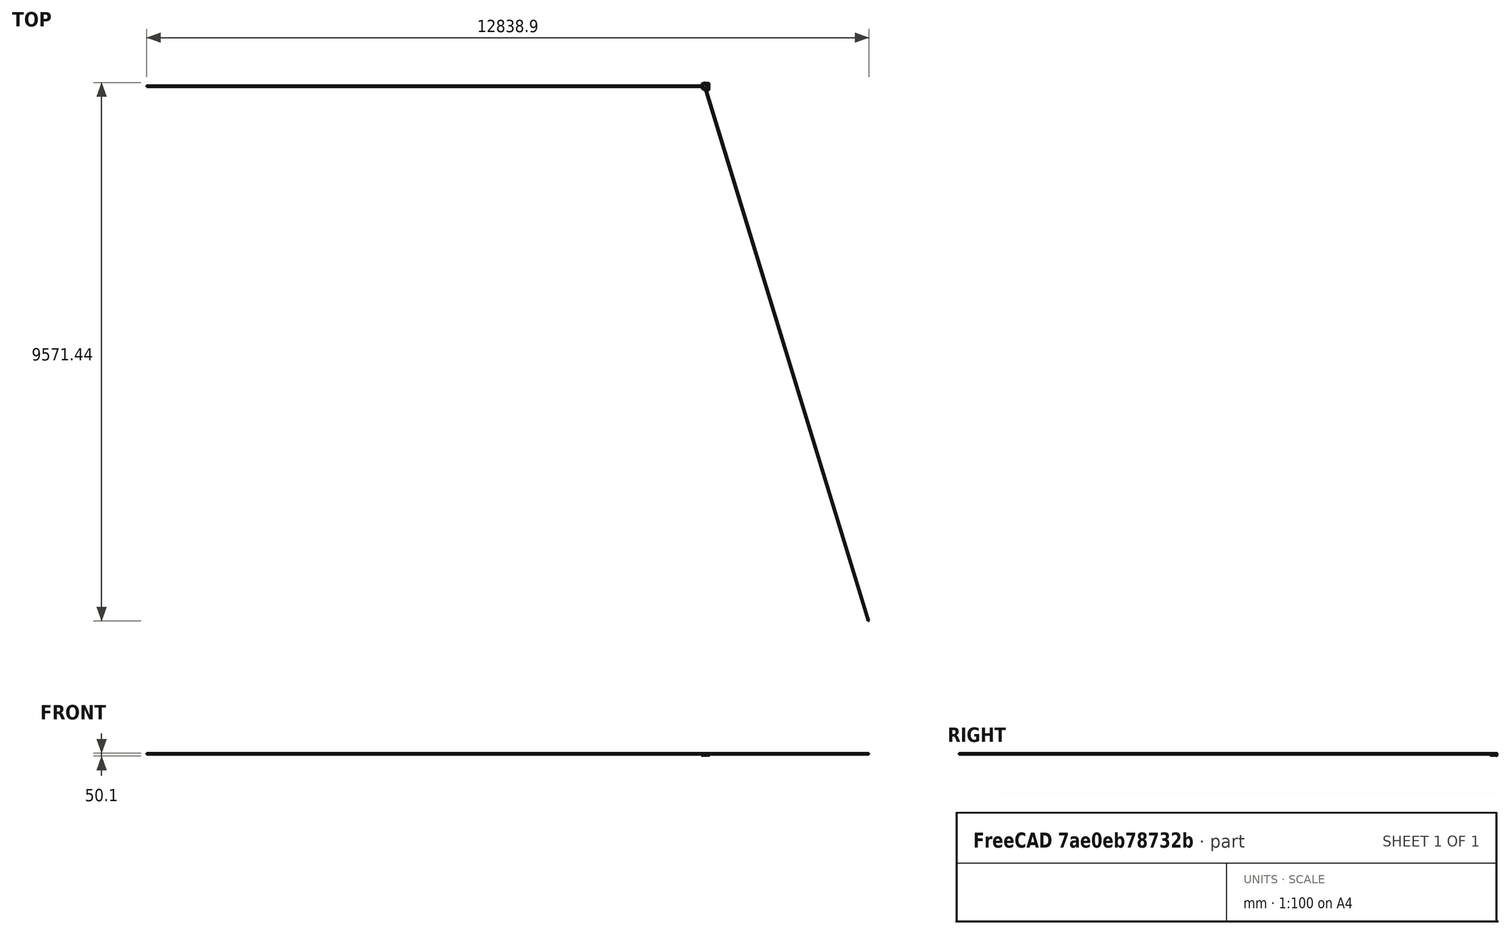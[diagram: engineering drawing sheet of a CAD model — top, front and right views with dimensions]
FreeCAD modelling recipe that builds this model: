
FCSTD DOCUMENT  (FreeCAD 0.16R)
Label: chainguard25TRearRev3
License: All rights reserved
LicenseURL: http://en.wikipedia.org/wiki/All_rights_reserved
objects: Sketcher::SketchObject×14, PartDesign::Pocket×7, PartDesign::Pad×6, Part::FeaturePython×4, Mesh::Feature×4, PartDesign::Fillet×2
note: 46 computed .brp shape members not serialized (recipe doc carries the construction recipe); baked Part::Feature solids carry a one-line shape summary decoded from their .brp

FEATURE [Sketcher::SketchObject] Sketch001
  sketch-geometry (7):
    g0: LineSegment StartX=60 StartY=64 StartZ=0 EndX=0 EndY=64 EndZ=0
    g1: LineSegment StartX=60 StartY=-64 StartZ=0 EndX=0 EndY=-64 EndZ=0
    g2: ArcOfCircle CenterX=8.21903e-05 CenterY=0 CenterZ=0 NormalX=0 NormalY=0 NormalZ=1 Radius=64 StartAngle=1.5708 EndAngle=4.71239
    g3: Circle CenterX=0 CenterY=0 CenterZ=0 NormalX=0 NormalY=0 NormalZ=1 Radius=45
    g4: ArcOfCircle CenterX=60 CenterY=51 CenterZ=0 NormalX=0 NormalY=0 NormalZ=1 Radius=13 StartAngle=0 EndAngle=1.5708
    g5: ArcOfCircle CenterX=60 CenterY=-51 CenterZ=0 NormalX=0 NormalY=0 NormalZ=1 Radius=13 StartAngle=4.71239 EndAngle=6.28319
    g6: LineSegment StartX=73 StartY=51 StartZ=0 EndX=73 EndY=-51 EndZ=0
  constraints (23):
    c: Horizontal(g0)
    c: Horizontal(g1)
    c: Coincident(g2,g1)
    c: Coincident(g0,g2)
    c: DistanceX(g1,g0) = 0
    c: Equal(g0,g1)
    c: DistanceY(g1,g0) = 128
    c: Radius(g2) = 64
    c: Symmetric(g1,g0,g-1)
    c: Radius(g3) = 45
    c: Coincident(g3,g-1)
    c: PointOnObject(g4,g0)
    c: Radius(g4) = 13
    c: DistanceX(g0,g0) = 60
    c: Equal(g5,g4)
    c: Vertical(g6)
    c: DistanceX(g-1,g6) = 73
    c: Symmetric(g6,g6,g-1)
    c: DistanceY(g6,g6) = 102
    c: Coincident(g4,g6)
    c: Coincident(g5,g6)
    c: Coincident(g1,g5)
    c: Coincident(g0,g4)
FEATURE [PartDesign::Pad] Pad  label="Faceplate"
  Length = 1.12
  Length2 = 100
  Reversed = true
  Sketch = -> Sketch001
  Type = 0
FEATURE [Sketcher::SketchObject] Sketch002
  sketch-geometry (8):
    g0: LineSegment StartX=60 StartY=64 StartZ=0 EndX=0 EndY=64 EndZ=0
    g1: LineSegment StartX=60 StartY=-64 StartZ=0 EndX=0 EndY=-64 EndZ=0
    g2: ArcOfCircle CenterX=6.44712e-05 CenterY=0 CenterZ=0 NormalX=0 NormalY=0 NormalZ=1 Radius=64 StartAngle=1.5708 EndAngle=4.71239
    g3: LineSegment StartX=0 StartY=62 StartZ=0 EndX=60 EndY=62 EndZ=0
    g4: LineSegment StartX=0 StartY=-62 StartZ=0 EndX=60 EndY=-62 EndZ=0
    g5: LineSegment StartX=60 StartY=64 StartZ=0 EndX=60 EndY=62 EndZ=0
    g6: LineSegment StartX=60 StartY=-62 StartZ=0 EndX=60 EndY=-64 EndZ=0
    g7: ArcOfCircle CenterX=1.45954e-05 CenterY=0 CenterZ=0 NormalX=0 NormalY=0 NormalZ=1 Radius=62 StartAngle=1.5708 EndAngle=4.71239
  constraints (25):
    c: Horizontal(g0)
    c: Horizontal(g1)
    c: Coincident(g2,g1)
    c: Coincident(g0,g2)
    c: DistanceX(g1,g0) = 0
    c: Equal(g0,g1)
    c: DistanceY(g1,g0) = 128
    c: Radius(g2) = 64
    c: Symmetric(g1,g0,g-1)
    c: Radius(g7) = 62
    c: Parallel(g0,g3)
    c: DistanceY(g3,g0) = 2
    c: DistanceY(g1,g4) = 2
    c: Parallel(g4,g1)
    c: DistanceX(g0,g3) = 0
    c: DistanceX(g4) = 0
    c: DistanceX(g0) = 60
    c: Equal(g3,g0)
    c: Equal(g4,g0)
    c: Coincident(g4,g6)
    c: Coincident(g6,g1)
    c: Coincident(g5,g3)
    c: Coincident(g5,g0)
    c: Coincident(g7,g3)
    c: Coincident(g7,g4)
FEATURE [PartDesign::Pad] Pad001  label="Connector"
  Length = 10
  Length2 = 100
  Sketch = -> Sketch002
  Type = 0
FEATURE [Sketcher::SketchObject] Sketch011
  Placement = pos=(0,64,0) rot=(0,0.707107,0.707107;3.14159rad)
  Support = -> Pad001 [Face1]
  sketch-geometry (4):
    g0: LineSegment StartX=-52 StartY=11 StartZ=0 EndX=-64.6477 EndY=14.0061 EndZ=0
    g1: LineSegment StartX=-64.6477 StartY=14.0061 StartZ=0 EndX=-60.9272 EndY=1.54985 EndZ=0
    g2: LineSegment StartX=-60.9272 StartY=1.54985 StartZ=0 EndX=-52 EndY=11 EndZ=0
    g3: Circle [constr] CenterX=-59.1916 CenterY=8.85198 CenterZ=0 NormalX=0 NormalY=0 NormalZ=1 Radius=7.50555
  constraints (14):
    c: Coincident(g0,g1)
    c: Coincident(g1,g2)
    c: Coincident(g2,g0)
    c: Equal(g0,g1)
    c: Equal(g0,g2)
    c: PointOnObject(g0,g3)
    c: PointOnObject(g1,g3)
    c: PointOnObject(g2,g3)
    c: DistanceY(g-1,g0) = 11
    c: DistanceX(g0,g-1) = 52
    c: Equal(g2,g0)
    c: Equal(g0,g1)
    c: Distance(g2) = 13
    c: Angle(g0) = 2.90824
FEATURE [PartDesign::Pocket] Pocket005  label="Bevel_connector"
  Length = 5
  Sketch = -> Sketch011
  Type = 1
FEATURE [Sketcher::SketchObject] Sketch017
  sketch-geometry (5):
    g0: LineSegment [constr] StartX=-4 StartY=2 StartZ=0 EndX=-27.8283 EndY=79.9388 EndZ=0
    g1: LineSegment StartX=-5.80278 StartY=67.752 StartZ=0 EndX=-39.2735 EndY=57.5189 EndZ=0
    g2: LineSegment StartX=-39.2735 StartY=57.5189 StartZ=0 EndX=-37.5192 EndY=51.7811 EndZ=0
    g3: LineSegment StartX=-37.5192 StartY=51.7811 StartZ=0 EndX=-4.04855 EndY=62.0141 EndZ=0
    g4: LineSegment StartX=-4.04855 StartY=62.0141 StartZ=0 EndX=-5.80278 EndY=67.752 EndZ=0
  constraints (15):
    c: DistanceY(g-1,g0) = 2
    c: DistanceX(g-1,g0) = -4
    c: Angle(g0) = 1.8675
    c: Coincident(g1,g2)
    c: Coincident(g2,g3)
    c: Coincident(g3,g4)
    c: Coincident(g1,g4)
    c: Parallel(g2,g4)
    c: Parallel(g1,g3)
    c: Perpendicular(g2,g1)
    c: Distance(g4) = 6
    c: Distance(g1) = 35
    c: Symmetric(g3,g2,g0)
    c: Distance(g-1,g1) = 68
    c: Distance(g0) = 81.5
FEATURE [Sketcher::SketchObject] Sketch020
  sketch-geometry (4):
    g0: LineSegment StartX=67 StartY=35 StartZ=0 EndX=73 EndY=35 EndZ=0
    g1: LineSegment StartX=73 StartY=35 StartZ=0 EndX=73 EndY=-25 EndZ=0
    g2: LineSegment StartX=73 StartY=-25 StartZ=0 EndX=67 EndY=-25 EndZ=0
    g3: LineSegment StartX=67 StartY=-25 StartZ=0 EndX=67 EndY=35 EndZ=0
  constraints (12):
    c: Coincident(g0,g1)
    c: Coincident(g1,g2)
    c: Coincident(g2,g3)
    c: Coincident(g3,g0)
    c: Horizontal(g0)
    c: Horizontal(g2)
    c: Vertical(g1)
    c: Vertical(g3)
    c: DistanceX(g-1,g0) = 73
    c: DistanceX(g0,g0) = 6
    c: DistanceY(g-1,g0) = 35
    c: DistanceY(g1,g1) = 60
FEATURE [PartDesign::Pad] Pad004  label="SyncBoss"
  Length = 31
  Length2 = 100
  Sketch = -> Sketch020
  Type = 0
FEATURE [Sketcher::SketchObject] Sketch021
  ExternalGeometry = -> [Pad004]
  Placement = pos=(73,0,0) rot=(0.57735,0.57735,0.57735;2.0944rad)
  Support = -> Pad004 [Face2]
  sketch-geometry (1):
    g0: Circle CenterX=5 CenterY=31 CenterZ=0 NormalX=0 NormalY=0 NormalZ=1 Radius=11.2
  constraints (2):
    c: Symmetric(g-4,g-3,g0)
    c: Radius(g0) = 11.2
FEATURE [PartDesign::Pocket] Pocket  label="SyncHole"
  Length = 5
  Sketch = -> Sketch021
  Type = 1
FEATURE [PartDesign::Pad] Pad005  label="STBoss"
  Length = 31
  Length2 = 1
  Sketch = -> Sketch017
  Type = 4
FEATURE [Sketcher::SketchObject] Sketch022
  ExternalGeometry = -> [Pad005]
  Placement = pos=(-19.4392,63.5829,0) rot=(-0.105093,0.703191,0.703191;3.35101rad)
  Support = -> Pad005 [Face1]
  sketch-geometry (1):
    g0: Circle CenterX=3.24048 CenterY=31 CenterZ=0 NormalX=0 NormalY=0 NormalZ=1 Radius=11.2
  constraints (2):
    c: Symmetric(g-4,g-3,g0)
    c: Radius(g0) = 11.2
FEATURE [PartDesign::Pocket] Pocket006  label="SThole"
  Length = 5
  Sketch = -> Sketch022
  Type = 1
FEATURE [Sketcher::SketchObject] Sketch023
  Placement = pos=(-19.4392,63.5829,0) rot=(-0.105093,0.703191,0.703191;3.35101rad)
  Support = -> Pocket006 [Face1]
  sketch-geometry (3):
    g0: LineSegment StartX=31.754 StartY=21.6568 StartZ=0 EndX=10.7035 EndY=-1 EndZ=0
    g1: LineSegment StartX=10.7035 StartY=-1 StartZ=0 EndX=40.8501 EndY=-7.90189 EndZ=0
    g2: LineSegment StartX=40.8501 StartY=-7.90189 StartZ=0 EndX=31.754 EndY=21.6568 EndZ=0
  constraints (9):
    c: Coincident(g0,g1)
    c: Coincident(g1,g2)
    c: Coincident(g0,g2)
    c: Equal(g0,g2)
    c: Equal(g2,g1)
    c: DistanceY(g0,g-1) = 1
    c: Angle(g1) = -0.225065
    c: Distance(g2) = 30.9266
    c: DistanceX(g-1,g0) = 10.7035
FEATURE [PartDesign::Pocket] Pocket007  label="STbevel1"
  Length = 6
  Sketch = -> Sketch023
  Type = 0
FEATURE [Sketcher::SketchObject] Sketch024
  sketch-geometry (6):
    g0: ArcOfCircle CenterX=0 CenterY=0 CenterZ=0 NormalX=0 NormalY=0 NormalZ=1 Radius=48 StartAngle=1.34179 EndAngle=4.9414
    g1: Circle CenterX=0 CenterY=0 CenterZ=0 NormalX=0 NormalY=0 NormalZ=1 Radius=45
    g2: LineSegment StartX=10.8966 StartY=46.7468 StartZ=0 EndX=65 EndY=35.4994 EndZ=0
    g3: LineSegment StartX=65 StartY=35.5006 StartZ=0 EndX=65 EndY=-35.4994 EndZ=0
    g4: LineSegment StartX=65 StartY=-35.4994 StartZ=0 EndX=10.8966 EndY=-46.7468 EndZ=0
    g5: LineSegment StartX=65 StartY=35.5 StartZ=0 EndX=65 EndY=-35.5 EndZ=0
  constraints (14):
    c: Coincident(g0,g-1)
    c: Radius(g0) = 48
    c: Coincident(g1,g-1)
    c: Radius(g1) = 45
    c: Coincident(g3,g4)
    c: Coincident(g0,g2)
    c: Distance(g3) = 71
    c: DistanceX(g-1,g2) = 65
    c: Equal(g4,g2)
    c: Vertical(g3)
    c: Symmetric(g2,g3,g-1)
    c: Distance(g2) = 55.2601
    c: DistanceY(g-1,g0) = 46.7468
    c: DistanceX(g0) = 10.8966
FEATURE [Sketcher::SketchObject] Sketch026
  sketch-geometry (4):
    g0: LineSegment StartX=0 StartY=47.5 StartZ=0 EndX=73 EndY=35 EndZ=0
    g1: LineSegment StartX=73 StartY=35 StartZ=0 EndX=73 EndY=-35 EndZ=0
    g2: LineSegment StartX=73 StartY=-35 StartZ=0 EndX=0 EndY=-47.5 EndZ=0
    g3: LineSegment StartX=0 StartY=-47.5 StartZ=0 EndX=0 EndY=47.5 EndZ=0
  constraints (11):
    c: Coincident(g0,g1)
    c: Coincident(g1,g2)
    c: Coincident(g2,g3)
    c: Coincident(g3,g0)
    c: Symmetric(g2,g0,g-1)
    c: Symmetric(g2,g0,g-1)
    c: Equal(g0,g2)
    c: Vertical(g1)
    c: DistanceY(g1,g1) = 70
    c: DistanceY(g3,g3) = 95
    c: DistanceX(g-1,g0) = 73
FEATURE [PartDesign::Pad] Pad007  label="FieldStiffener"
  Length = 1
  Length2 = 100
  Sketch = -> Sketch026
  Type = 0
FEATURE [Sketcher::SketchObject] Sketch028
  ExternalGeometry = -> [Pocket]
  Placement = pos=(0,0,31) rot=(0,0,1;0rad)
  Support = -> Pocket [Face5]
  sketch-geometry (2):
    g0: Circle CenterX=70 CenterY=19 CenterZ=0 NormalX=0 NormalY=0 NormalZ=1 Radius=0.8
    g1: Circle CenterX=70 CenterY=-9 CenterZ=0 NormalX=0 NormalY=0 NormalZ=1 Radius=0.8
  constraints (6):
    c: DistanceY(g-4,g0) = 2.8
    c: DistanceX(g0,g-4) = 3
    c: DistanceX(g1,g-6) = 3
    c: DistanceY(g1,g-5) = 2.8
    c: Equal(g1,g0)
    c: Radius(g1) = 0.8
FEATURE [PartDesign::Pocket] Pocket010  label="SyncScrewHoles"
  Length = 15
  Sketch = -> Sketch028
  Type = 0
FEATURE [Sketcher::SketchObject] Sketch029
  ExternalGeometry = -> [Pocket010]
  Placement = pos=(73,0,0) rot=(0.57735,0.57735,0.57735;2.0944rad)
  Support = -> Pocket010 [Face3]
  sketch-geometry (6):
    g0: LineSegment StartX=35 StartY=3 StartZ=0 EndX=22.5 EndY=32 EndZ=0
    g1: LineSegment StartX=22.5 StartY=32 StartZ=0 EndX=-12.5 EndY=32 EndZ=0
    g2: LineSegment StartX=-12.5 StartY=32 StartZ=0 EndX=-25 EndY=3 EndZ=0
    g3: LineSegment StartX=-25 StartY=3 StartZ=0 EndX=-28.2949 EndY=52.1665 EndZ=0
    g4: LineSegment StartX=-28.2949 StartY=52.1665 StartZ=0 EndX=43.0613 EndY=52.1665 EndZ=0
    g5: LineSegment StartX=43.0613 StartY=52.1665 StartZ=0 EndX=35 EndY=3 EndZ=0
  constraints (18):
    c: Coincident(g0,g1)
    c: Horizontal(g1)
    c: Coincident(g1,g2)
    c: Coincident(g2,g3)
    c: Coincident(g3,g4)
    c: Horizontal(g4)
    c: Coincident(g4,g5)
    c: Coincident(g0,g5)
    c: DistanceX(g-4,g0) = 6.3
    c: DistanceX(g1,g-4) = 6.3
    c: DistanceX(g-3,g0) = 0
    c: DistanceX(g2,g-6) = 0
    c: DistanceX(g4,g4) = 71.3562
    c: Distance(g3) = 49.2768
    c: Distance(g5) = 49.823
    c: DistanceY(g-4,g1) = 1
    c: DistanceY(g-6,g2) = 3
    c: DistanceY(g-3,g0) = 3
FEATURE [PartDesign::Pocket] Pocket011  label="SyncBigBevel"
  Length = 5
  Sketch = -> Sketch029
  Type = 1
FEATURE [Sketcher::SketchObject] Sketch
  ExternalGeometry = -> [Pad]
  Support = -> Pad [Face8]
  sketch-geometry (5):
    g0: Circle CenterX=0 CenterY=0 CenterZ=0 NormalX=0 NormalY=0 NormalZ=1 Radius=45
    g1: ArcOfCircle CenterX=0 CenterY=0 CenterZ=0 NormalX=0 NormalY=0 NormalZ=1 Radius=48 StartAngle=1.45745 EndAngle=4.82574
    g2: LineSegment StartX=5.42905 StartY=47.692 StartZ=0 EndX=73 EndY=40 EndZ=0
    g3: LineSegment StartX=73 StartY=40 StartZ=0 EndX=73 EndY=-40 EndZ=0
    g4: LineSegment StartX=73 StartY=-40 StartZ=0 EndX=5.42905 EndY=-47.692 EndZ=0
  constraints (14):
    c: Coincident(g2,g3)
    c: Vertical(g3)
    c: Coincident(g3,g4)
    c: Coincident(g0,g-1)
    c: Coincident(g1,g-1)
    c: Radius(g0) = 45
    c: Radius(g1) = 48
    c: DistanceX(g-3,g2) = 0
    c: DistanceY(g3,g-1) = 40
    c: DistanceY(g-1,g2) = 40
    c: Coincident(g1,g2)
    c: Coincident(g1,g4)
    c: Symmetric(g1,g1,g-1)
    c: DistanceX(g-1,g1) = 5.42905
FEATURE [PartDesign::Pad] Pad008  label="FaceStiffener"
  Length = 1
  Length2 = 100
  Sketch = -> Sketch
  Type = 0
FEATURE [PartDesign::Fillet] Fillet  label="SyncFillets"
  Base = -> Pocket011 [Edge13,Edge14,Edge15,Edge3,Edge9,Edge21,Edge19,Edge22]
  Radius = 1
FEATURE [Sketcher::SketchObject] Sketch030
  ExternalGeometry = -> [Pocket007]
  Placement = pos=(0,0,31) rot=(0,0,1;0rad)
  Support = -> Pocket007 [Face5]
  sketch-geometry (2):
    g0: Circle CenterX=-35.384 CenterY=55.571 CenterZ=0 NormalX=0 NormalY=0 NormalZ=1 Radius=0.8
    g1: Circle CenterX=-7.93803 CenterY=63.9621 CenterZ=0 NormalX=0 NormalY=0 NormalZ=1 Radius=0.8
  constraints (4):
    c: Equal(g0,g1)
    c: Radius(g0) = 0.8
    c: Symmetric(g-3,g-6,g1)
    c: Symmetric(g-4,g-9,g0)
FEATURE [PartDesign::Pocket] Pocket012
  Length = 15
  Sketch = -> Sketch030
  Type = 0
FEATURE [PartDesign::Fillet] Fillet001  label="STfillets"
  Base = -> Pocket012 [Edge23,Edge7,Edge8,Edge20,Edge12,Edge13,Edge14,Edge3,Edge2,Edge10,Edge11,Edge9,Edge1]
  Radius = 1
FEATURE [Part::FeaturePython] refine  label="refine_FaceStiffener"  # WARN: FeaturePython — macro-defined, semantics opaque (R4)
  Base = -> Pad008
FEATURE [Part::FeaturePython] refine001  label="refine_Bevel_connector"  # WARN: FeaturePython — macro-defined, semantics opaque (R4)
  Base = -> Pocket005
FEATURE [Part::FeaturePython] refine002  label="refine_SyncFillets"  # WARN: FeaturePython — macro-defined, semantics opaque (R4)
  Base = -> Fillet
FEATURE [Part::FeaturePython] refine003  label="refine_STfillets"  # WARN: FeaturePython — macro-defined, semantics opaque (R4)
  Base = -> Fillet001
FEATURE [Mesh::Feature] Mesh  label="refine_FaceStiffener (Meshed)"
FEATURE [Mesh::Feature] Mesh001  label="refine_Bevel_connector (Meshed)"
FEATURE [Mesh::Feature] Mesh002  label="refine_SyncFillets (Meshed)"
FEATURE [Mesh::Feature] Mesh003  label="refine_STfillets (Meshed)"
